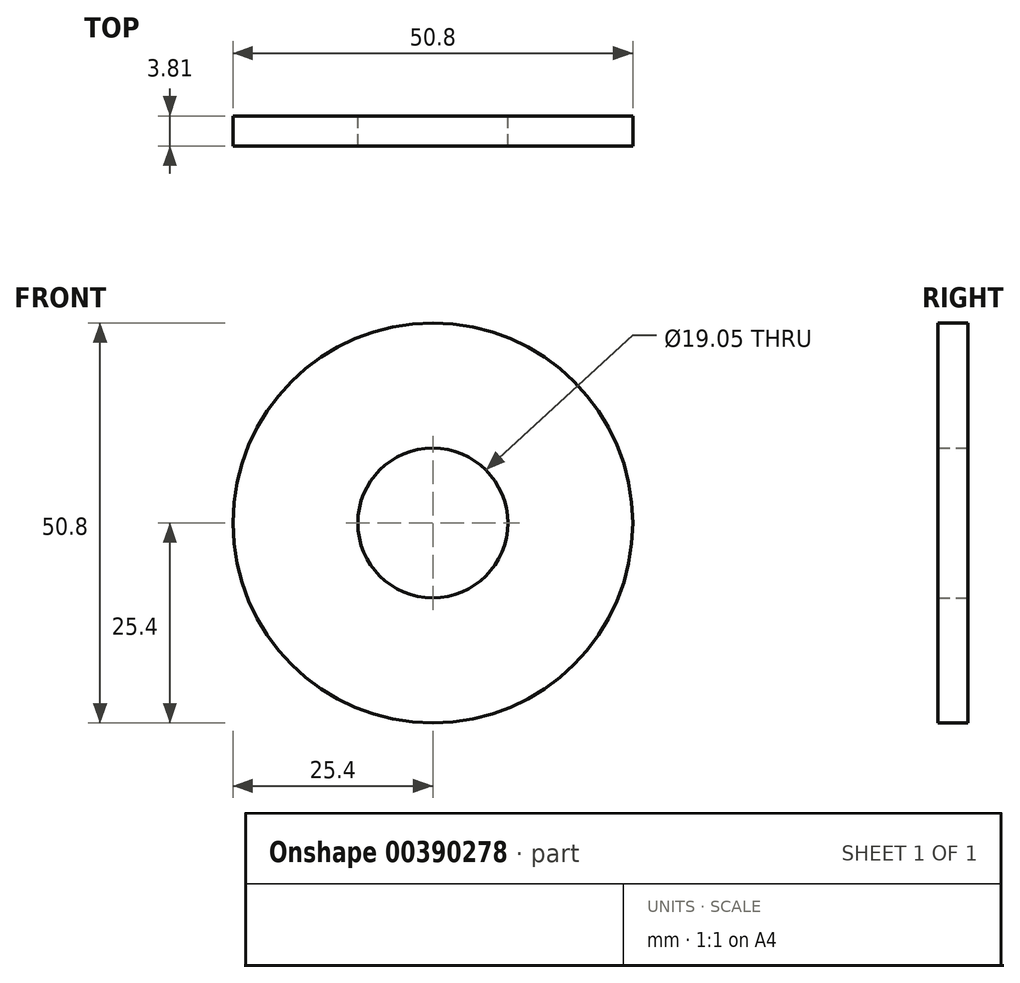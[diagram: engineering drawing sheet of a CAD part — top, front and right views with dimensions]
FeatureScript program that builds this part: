
annotation { "Feature Type Name" : "Feature", "Feature Type Description" : "" }
export const myFeature = defineFeature(function(context is Context, id is Id, definition is map)
    precondition{}
    {
        {
            var Q0;
            Q0=qCreatedBy(makeId("Front.planeOp"),FACE);
            var sketch = newSketch(context, id + "F0", { "sketchPlane" : qUnion([Q0])});
            skCircle(sketch, "E0", {"center": v(0, 0) * mm, "radius": 25.4 * mm});
            skCircle(sketch, "E1", {"center": v(0, 0) * mm, "radius": 9.53 * mm});
            skSolve(sketch);
        }
        {
            var Q0;
            Q0=makeQuery(id+"F0.imprint","IMPRINT",FACE,{"disambiguationData":[TD([[makeQuery(id+"F0.imprint","IMPRINT",EDGE,{"derivedFrom":sQuery(id+"F0.wireOp",EDGE,"E0")}),1.0]])]});
            extrude(context, id + "F1", {"entities" : qUnion([Q0]), "depth" : 3.8 * mm});
        }
    });
